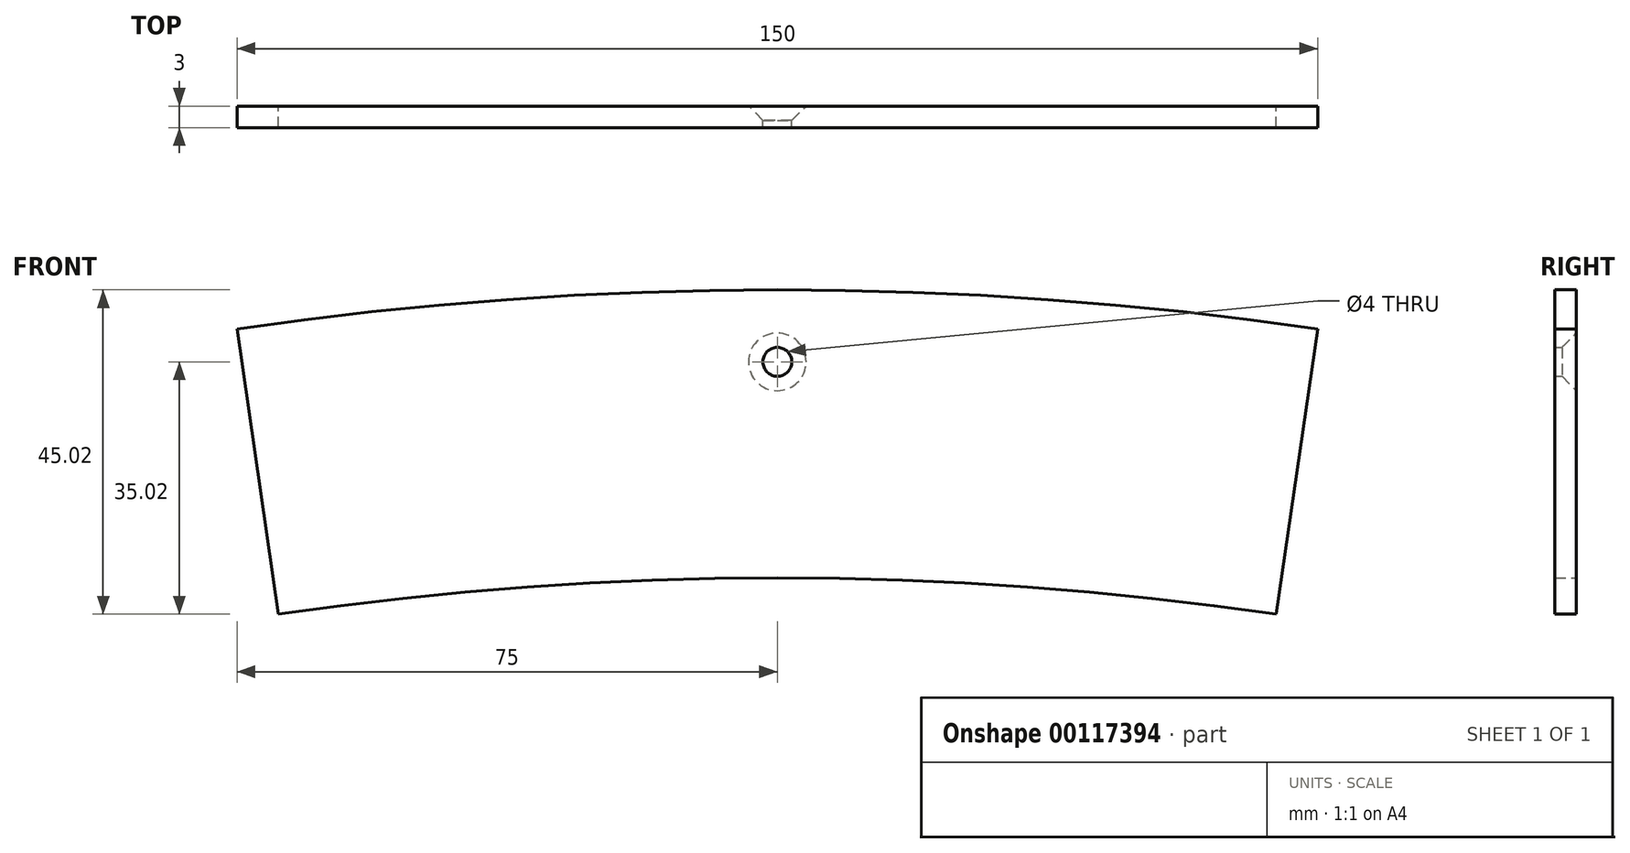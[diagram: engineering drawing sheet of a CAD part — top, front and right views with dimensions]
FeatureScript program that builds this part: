
annotation { "Feature Type Name" : "Feature", "Feature Type Description" : "" }
export const myFeature = defineFeature(function(context is Context, id is Id, definition is map)
    precondition{}
    {
        {
            var Q0;
            Q0=qCreatedBy(makeId("Front.planeOp"),FACE);
            var sketch = newSketch(context, id + "F0", { "sketchPlane" : qUnion([Q0])});
            skCircle(sketch, "E0", {"center": v(0, 0) * mm, "radius": 500 * mm, "construction": true});
            skLineSegment(sketch, "E1", {"start": v(-500, 0) * mm, "end": v(500, 0) * mm, "construction": true});
            skLineSegment(sketch, "E2", {"start": v(0, 510) * mm, "end": v(0, -500) * mm, "construction": true});
            skCircle(sketch, "E3", {"center": v(0, 0) * mm, "radius": 480 * mm});
            skCircle(sketch, "E4", {"center": v(0, 0) * mm, "radius": 520 * mm});
            skLineSegment(sketch, "E5", {"start": v(0, 0) * mm, "end": v(-504.75, 125) * mm});
            skLineSegment(sketch, "E6", {"start": v(0, 0) * mm, "end": v(-504.75, -125) * mm});
            skLineSegment(sketch, "E7", {"start": v(0, 0) * mm, "end": v(75, 514.56) * mm});
            skLineSegment(sketch, "E8", {"start": v(0, 0) * mm, "end": v(-75, 514.56) * mm});
            skCircle(sketch, "E9", {"center": v(-45, 508.01) * mm, "radius": 2 * mm});
            skCircle(sketch, "E10", {"center": v(45, 508.01) * mm, "radius": 2 * mm});
            skCircle(sketch, "E11", {"center": v(0, 0) * mm, "radius": 510 * mm, "construction": true});
            skSolve(sketch);
        }
        {
            var Q0;
            Q0=makeQuery(id+"F0.imprint","IMPRINT",FACE,{"disambiguationData":[TD([[makeQuery(id+"F0.imprint","IMPRINT",EDGE,{"derivedFrom":sQuery(id+"F0.wireOp",EDGE,"E9")}),-1.0]])]});
            var Q1;
            Q1=makeQuery(id+"F0.imprint","IMPRINT",FACE,{"disambiguationData":[TD([[makeQuery(id+"F0.imprint","IMPRINT",EDGE,{"derivedFrom":sQuery(id+"F0.wireOp",EDGE,"E9")}),1.0]])]});
            var Q2;
            Q2=makeQuery(id+"F0.imprint","IMPRINT",FACE,{"disambiguationData":[TD([[makeQuery(id+"F0.imprint","IMPRINT",EDGE,{"derivedFrom":sQuery(id+"F0.wireOp",EDGE,"E10")}),1.0]])]});
            extrude(context, id + "F1", {"entities" : qUnion([Q0, Q1, Q2]), "depth" : 3 * mm});
        }
        {
            var Q0;
            Q0=sQuery(id+"F0.wireOp",VERTEX,"E2.start");
            var Q1;
            Q1=makeQuery(id+"F1.opExtrude","SWEPT_BODY",BODY,{"disambiguationData":[OSD([sQuery(id+"F0.wireOp",EDGE,"E3"),sQuery(id+"F0.wireOp",EDGE,"E4"),sQuery(id+"F0.wireOp",EDGE,"E7"),sQuery(id+"F0.wireOp",EDGE,"E8")])]});
            hole(context, id + "F2", {"style" : HoleStyle.C_SINK, "endStyle" : HoleEndStyle.THROUGH, "oppositeDirection" : true, "holeDiameter" : 4 * mm, "cSinkDiameter" : 8 * mm, "cSinkAngle" : 90 * degree, "isTappedThrough" : true, "tappedDepth" : 12 * mm, "tapClearance" : 3, "locations" : qUnion([Q0]), "scope" : qUnion([Q1])});
        }
    });
